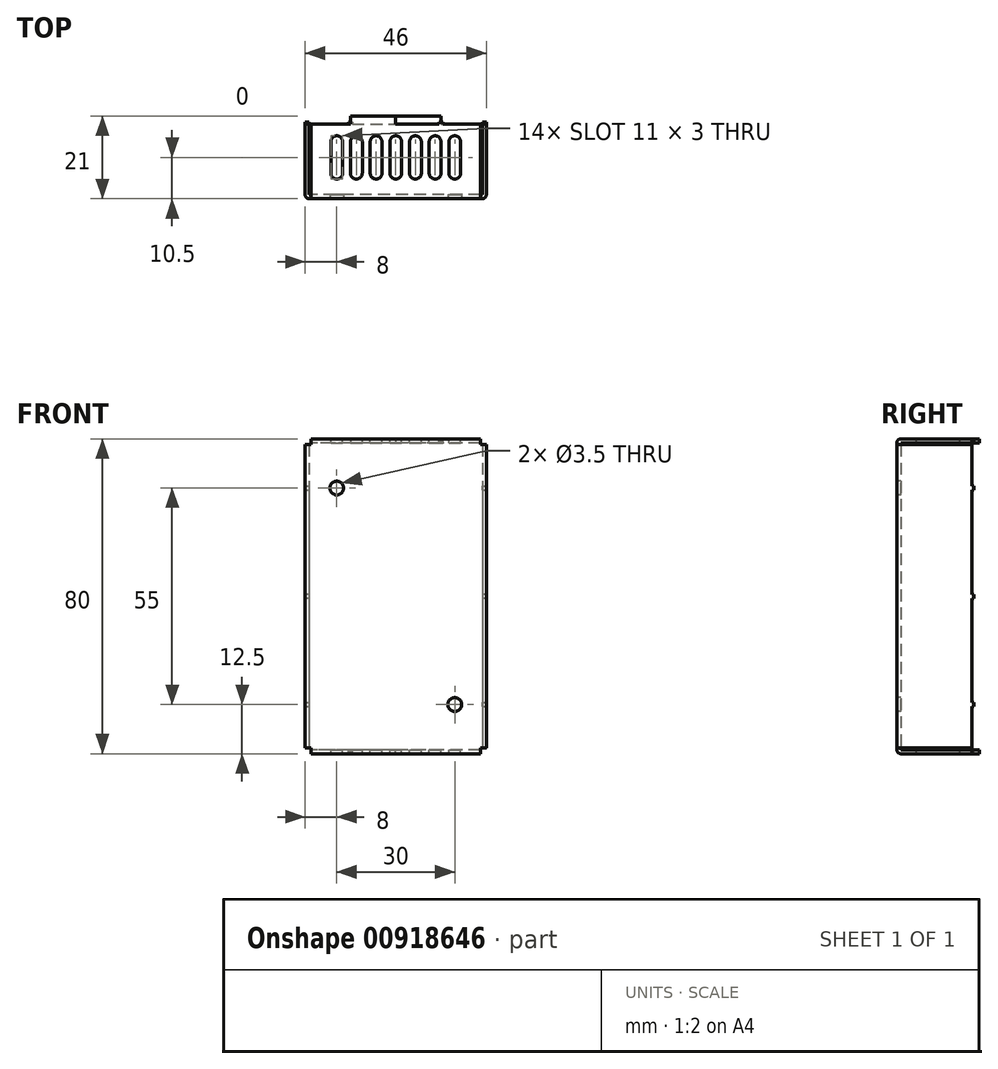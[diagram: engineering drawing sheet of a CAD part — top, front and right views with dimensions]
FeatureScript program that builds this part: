
annotation { "Feature Type Name" : "Feature", "Feature Type Description" : "" }
export const myFeature = defineFeature(function(context is Context, id is Id, definition is map)
    precondition{}
    {
        {
            var Q0;
            Q0=qCreatedBy(makeId("Front.planeOp"),FACE);
            var sketch = newSketch(context, id + "F0", { "sketchPlane" : qUnion([Q0])});
            skLineSegment(sketch, "E0.bottom", {"start": v(-23, 40) * mm, "end": v(23, 40) * mm});
            skLineSegment(sketch, "E0.top", {"start": v(-23, -40) * mm, "end": v(23, -40) * mm});
            skLineSegment(sketch, "E0.left", {"start": v(-23, 40) * mm, "end": v(-23, -40) * mm});
            skLineSegment(sketch, "E0.right", {"start": v(23, 40) * mm, "end": v(23, -40) * mm});
            skPoint(sketch, "E1", {"position": v(23, 0) * mm});
            skPoint(sketch, "E2", {"position": v(0, 40) * mm});
            skSolve(sketch);
        }
        {
            var Q0;
            Q0 = qSketchRegion(id + "F0", true);
            extrude(context, id + "F1", {"entities" : qUnion([Q0]), "oppositeDirection" : true, "depth" : 1 * mm, "offsetDistance" : 25 * mm});
        }
        {
            var Q0;
            Q0=makeQuery(id+"F1.opExtrude","CAP_FACE",FACE,{"disambiguationData":[OSD([sQuery(id+"F0.wireOp",EDGE,"E0.bottom"),sQuery(id+"F0.wireOp",EDGE,"E0.top"),sQuery(id+"F0.wireOp",EDGE,"E0.left"),sQuery(id+"F0.wireOp",EDGE,"E0.right")])],"isStart":false});
            var sketch = newSketch(context, id + "F2", { "sketchPlane" : qUnion([Q0])});
            skLineSegment(sketch, "E3.bottom", {"start": v(-21.5, 40) * mm, "end": v(21.5, 40) * mm});
            skLineSegment(sketch, "E3.top", {"start": v(-21.5, 39) * mm, "end": v(21.5, 39) * mm});
            skLineSegment(sketch, "E3.left", {"start": v(-21.5, 40) * mm, "end": v(-21.5, 39) * mm});
            skLineSegment(sketch, "E3.right", {"start": v(21.5, 40) * mm, "end": v(21.5, 39) * mm});
            skLineSegment(sketch, "E4.bottom", {"start": v(-23, 38.5) * mm, "end": v(-22, 38.5) * mm});
            skLineSegment(sketch, "E4.top", {"start": v(-23, -38.5) * mm, "end": v(-22, -38.5) * mm});
            skLineSegment(sketch, "E4.left", {"start": v(-23, 38.5) * mm, "end": v(-23, -38.5) * mm});
            skLineSegment(sketch, "E4.right", {"start": v(-22, 38.5) * mm, "end": v(-22, -38.5) * mm});
            skLineSegment(sketch, "E5.bottom", {"start": v(23, 38.5) * mm, "end": v(22, 38.5) * mm});
            skLineSegment(sketch, "E5.top", {"start": v(23, -38.5) * mm, "end": v(22, -38.5) * mm});
            skLineSegment(sketch, "E5.left", {"start": v(23, 38.5) * mm, "end": v(23, -38.5) * mm});
            skLineSegment(sketch, "E5.right", {"start": v(22, 38.5) * mm, "end": v(22, -38.5) * mm});
            skLineSegment(sketch, "E6.bottom", {"start": v(-21.5, -39) * mm, "end": v(21.5, -39) * mm});
            skLineSegment(sketch, "E6.top", {"start": v(-21.5, -40) * mm, "end": v(21.5, -40) * mm});
            skLineSegment(sketch, "E6.left", {"start": v(-21.5, -39) * mm, "end": v(-21.5, -40) * mm});
            skLineSegment(sketch, "E6.right", {"start": v(21.5, -39) * mm, "end": v(21.5, -40) * mm});
            skSolve(sketch);
        }
        {
            var Q0;
            Q0 = qSketchRegion(id + "F2", true);
            extrude(context, id + "F3", {"entities" : qUnion([Q0]), "operationType" : NewBodyOperationType.ADD, "depth" : 18 * mm, "offsetDistance" : 25 * mm});
        }
        {
            var Q0;
            Q0=makeQuery(id+"F1.opExtrude","CAP_FACE",FACE,{"disambiguationData":[OSD([sQuery(id+"F0.wireOp",EDGE,"E0.bottom"),sQuery(id+"F0.wireOp",EDGE,"E0.top"),sQuery(id+"F0.wireOp",EDGE,"E0.left"),sQuery(id+"F0.wireOp",EDGE,"E0.right")])],"isStart":false});
            var sketch = newSketch(context, id + "F4", { "sketchPlane" : qUnion([Q0])});
            skLineSegment(sketch, "E7.bottom", {"start": v(21.5, 40) * mm, "end": v(23, 40) * mm});
            skLineSegment(sketch, "E7.top", {"start": v(21.5, 38.5) * mm, "end": v(23, 38.5) * mm});
            skLineSegment(sketch, "E7.left", {"start": v(21.5, 40) * mm, "end": v(21.5, 38.5) * mm});
            skLineSegment(sketch, "E7.right", {"start": v(23, 40) * mm, "end": v(23, 38.5) * mm});
            skLineSegment(sketch, "E8.bottom", {"start": v(-23, 38.5) * mm, "end": v(-21.5, 38.5) * mm});
            skLineSegment(sketch, "E8.top", {"start": v(-23, 40) * mm, "end": v(-21.5, 40) * mm});
            skLineSegment(sketch, "E8.left", {"start": v(-23, 38.5) * mm, "end": v(-23, 40) * mm});
            skLineSegment(sketch, "E8.right", {"start": v(-21.5, 38.5) * mm, "end": v(-21.5, 40) * mm});
            skLineSegment(sketch, "E9.bottom", {"start": v(21.5, -40) * mm, "end": v(23, -40) * mm});
            skLineSegment(sketch, "E9.top", {"start": v(21.5, -38.5) * mm, "end": v(23, -38.5) * mm});
            skLineSegment(sketch, "E9.left", {"start": v(21.5, -40) * mm, "end": v(21.5, -38.5) * mm});
            skLineSegment(sketch, "E9.right", {"start": v(23, -40) * mm, "end": v(23, -38.5) * mm});
            skLineSegment(sketch, "E10.bottom", {"start": v(-23, -38.5) * mm, "end": v(-21.5, -38.5) * mm});
            skLineSegment(sketch, "E10.top", {"start": v(-23, -40) * mm, "end": v(-21.5, -40) * mm});
            skLineSegment(sketch, "E10.left", {"start": v(-23, -38.5) * mm, "end": v(-23, -40) * mm});
            skLineSegment(sketch, "E10.right", {"start": v(-21.5, -38.5) * mm, "end": v(-21.5, -40) * mm});
            skSolve(sketch);
        }
        {
            var Q0;
            Q0 = qSketchRegion(id + "F4", true);
            extrude(context, id + "F5", {"entities" : qUnion([Q0]), "operationType" : NewBodyOperationType.REMOVE, "endBound" : BoundingType.THROUGH_ALL, "oppositeDirection" : true, "depth" : 25 * mm, "offsetDistance" : 25 * mm});
        }
        {
            var Q0;
            Q0=makeQuery(id+"F1.opExtrude","CAP_FACE",FACE,{"disambiguationData":[OSD([sQuery(id+"F0.wireOp",EDGE,"E0.bottom"),sQuery(id+"F0.wireOp",EDGE,"E0.top"),sQuery(id+"F0.wireOp",EDGE,"E0.left"),sQuery(id+"F0.wireOp",EDGE,"E0.right")])],"isStart":true});
            var sketch = newSketch(context, id + "F6", { "sketchPlane" : qUnion([Q0])});
            skCircle(sketch, "E11", {"center": v(15, -27.5) * mm, "radius": 1.75 * mm});
            skCircle(sketch, "E12", {"center": v(-15, 27.5) * mm, "radius": 1.75 * mm});
            skSolve(sketch);
        }
        {
            var Q0;
            Q0 = qSketchRegion(id + "F6", true);
            extrude(context, id + "F7", {"entities" : qUnion([Q0]), "operationType" : NewBodyOperationType.REMOVE, "endBound" : BoundingType.THROUGH_ALL, "oppositeDirection" : true, "depth" : 25 * mm, "offsetDistance" : 25 * mm});
        }
        {
            var Q0;
            Q0=makeQuery(id+"F3.boolean.opBoolean","MERGE",FACE,{"derivedFrom":[makeQuery(id+"F1.opExtrude","SWEPT_FACE",FACE,{"disambiguationData":[OSD([sQuery(id+"F0.wireOp",EDGE,"E0.bottom")])]}),makeQuery(id+"F3.opExtrude","SWEPT_FACE",FACE,{"disambiguationData":[OSD([sQuery(id+"F2.wireOp",EDGE,"E3.bottom")])]})]});
            var sketch = newSketch(context, id + "F8", { "sketchPlane" : qUnion([Q0])});
            skLineSegment(sketch, "E13.left", {"start": v(1.5, 6.5) * mm, "end": v(1.5, 14.5) * mm});
            skLineSegment(sketch, "E13.right", {"start": v(-1.5, 6.5) * mm, "end": v(-1.5, 14.5) * mm});
            skArc(sketch, "E14", {"start": v(-1.5, 6.5) * mm, "mid": v(0, 5) * mm, "end": v(1.5, 6.5) * mm});
            skArc(sketch, "E15", {"start": v(1.5, 14.5) * mm, "mid": v(0, 16) * mm, "end": v(-1.5, 14.5) * mm});
            skPoint(sketch, "E16", {"position": v(0, 5) * mm});
            skPoint(sketch, "E17", {"position": v(0, 16) * mm});
            skLineSegment(sketch, "E18.left", {"start": v(-3.5, 6.5) * mm, "end": v(-3.5, 14.5) * mm});
            skLineSegment(sketch, "E18.right", {"start": v(-6.5, 6.5) * mm, "end": v(-6.5, 14.5) * mm});
            skArc(sketch, "E19", {"start": v(-6.5, 6.5) * mm, "mid": v(-5, 5) * mm, "end": v(-3.5, 6.5) * mm});
            skArc(sketch, "E20", {"start": v(-3.5, 14.5) * mm, "mid": v(-5, 16) * mm, "end": v(-6.5, 14.5) * mm});
            skPoint(sketch, "E21", {"position": v(-5, 5) * mm});
            skPoint(sketch, "E22", {"position": v(-5, 16) * mm});
            skLineSegment(sketch, "E23.left", {"start": v(-8.5, 6.5) * mm, "end": v(-8.5, 14.5) * mm});
            skLineSegment(sketch, "E23.right", {"start": v(-11.5, 6.5) * mm, "end": v(-11.5, 14.5) * mm});
            skArc(sketch, "E24", {"start": v(-11.5, 6.5) * mm, "mid": v(-10, 5) * mm, "end": v(-8.5, 6.5) * mm});
            skArc(sketch, "E25", {"start": v(-8.5, 14.5) * mm, "mid": v(-10, 16) * mm, "end": v(-11.5, 14.5) * mm});
            skPoint(sketch, "E26", {"position": v(-10, 5) * mm});
            skPoint(sketch, "E27", {"position": v(-10, 16) * mm});
            skLineSegment(sketch, "E28.left", {"start": v(-13.5, 6.5) * mm, "end": v(-13.5, 14.5) * mm});
            skLineSegment(sketch, "E28.right", {"start": v(-16.5, 6.5) * mm, "end": v(-16.5, 14.5) * mm});
            skArc(sketch, "E29", {"start": v(-16.5, 6.5) * mm, "mid": v(-15, 5) * mm, "end": v(-13.5, 6.5) * mm});
            skArc(sketch, "E30", {"start": v(-13.5, 14.5) * mm, "mid": v(-15, 16) * mm, "end": v(-16.5, 14.5) * mm});
            skPoint(sketch, "E31", {"position": v(-15, 5) * mm});
            skPoint(sketch, "E32", {"position": v(-15, 16) * mm});
            skLineSegment(sketch, "E33.left", {"start": v(11.5, 6.5) * mm, "end": v(11.5, 14.5) * mm});
            skLineSegment(sketch, "E33.right", {"start": v(8.5, 6.5) * mm, "end": v(8.5, 14.5) * mm});
            skArc(sketch, "E34", {"start": v(8.5, 6.5) * mm, "mid": v(10, 5) * mm, "end": v(11.5, 6.5) * mm});
            skArc(sketch, "E35", {"start": v(11.5, 14.5) * mm, "mid": v(10, 16) * mm, "end": v(8.5, 14.5) * mm});
            skPoint(sketch, "E36", {"position": v(10, 5) * mm});
            skPoint(sketch, "E37", {"position": v(10, 16) * mm});
            skLineSegment(sketch, "E38.left", {"start": v(6.5, 6.5) * mm, "end": v(6.5, 14.5) * mm});
            skLineSegment(sketch, "E38.right", {"start": v(3.5, 6.5) * mm, "end": v(3.5, 14.5) * mm});
            skArc(sketch, "E39", {"start": v(3.5, 6.5) * mm, "mid": v(5, 5) * mm, "end": v(6.5, 6.5) * mm});
            skArc(sketch, "E40", {"start": v(6.5, 14.5) * mm, "mid": v(5, 16) * mm, "end": v(3.5, 14.5) * mm});
            skPoint(sketch, "E41", {"position": v(5, 5) * mm});
            skPoint(sketch, "E42", {"position": v(5, 16) * mm});
            skLineSegment(sketch, "E43.left", {"start": v(16.5, 6.5) * mm, "end": v(16.5, 14.5) * mm});
            skLineSegment(sketch, "E43.right", {"start": v(13.5, 6.5) * mm, "end": v(13.5, 14.5) * mm});
            skArc(sketch, "E44", {"start": v(13.5, 6.5) * mm, "mid": v(15, 5) * mm, "end": v(16.5, 6.5) * mm});
            skArc(sketch, "E45", {"start": v(16.5, 14.5) * mm, "mid": v(15, 16) * mm, "end": v(13.5, 14.5) * mm});
            skPoint(sketch, "E46", {"position": v(15, 5) * mm});
            skPoint(sketch, "E47", {"position": v(15, 16) * mm});
            skSolve(sketch);
        }
        {
            var Q0;
            Q0 = qSketchRegion(id + "F8", true);
            extrude(context, id + "F9", {"entities" : qUnion([Q0]), "operationType" : NewBodyOperationType.REMOVE, "endBound" : BoundingType.THROUGH_ALL, "oppositeDirection" : true, "depth" : 25 * mm, "offsetDistance" : 25 * mm});
        }
        {
            var Q0;
            Q0=makeQuery(id+"F3.opExtrude","CAP_FACE",FACE,{"disambiguationData":[OSD([sQuery(id+"F2.wireOp",EDGE,"E6.bottom"),sQuery(id+"F2.wireOp",EDGE,"E6.top"),sQuery(id+"F2.wireOp",EDGE,"E6.left"),sQuery(id+"F2.wireOp",EDGE,"E6.right")])],"isStart":false});
            var sketch = newSketch(context, id + "F10", { "sketchPlane" : qUnion([Q0])});
            skLineSegment(sketch, "E48.bottom", {"start": v(0, -40) * mm, "end": v(-11.5, -40) * mm});
            skLineSegment(sketch, "E48.top", {"start": v(0, -39) * mm, "end": v(-11.5, -39) * mm});
            skLineSegment(sketch, "E48.left", {"start": v(0, -40) * mm, "end": v(0, -39) * mm});
            skLineSegment(sketch, "E48.right", {"start": v(-11.5, -40) * mm, "end": v(-11.5, -39) * mm});
            skLineSegment(sketch, "E49.bottom", {"start": v(0, 40) * mm, "end": v(11.5, 40) * mm});
            skLineSegment(sketch, "E49.top", {"start": v(0, 39) * mm, "end": v(11.5, 39) * mm});
            skLineSegment(sketch, "E49.left", {"start": v(0, 40) * mm, "end": v(0, 39) * mm});
            skLineSegment(sketch, "E49.right", {"start": v(11.5, 40) * mm, "end": v(11.5, 39) * mm});
            skSolve(sketch);
        }
        {
            var Q0;
            Q0 = qSketchRegion(id + "F10", true);
            extrude(context, id + "F11", {"entities" : qUnion([Q0]), "operationType" : NewBodyOperationType.ADD, "depth" : 2 * mm, "offsetDistance" : 25 * mm});
        }
        {
            var Q0;
            Q0=makeQuery(id+"F3.opExtrude","CAP_FACE",FACE,{"disambiguationData":[OSD([sQuery(id+"F2.wireOp",EDGE,"E5.bottom"),sQuery(id+"F2.wireOp",EDGE,"E5.top"),sQuery(id+"F2.wireOp",EDGE,"E5.left"),sQuery(id+"F2.wireOp",EDGE,"E5.right")])],"isStart":false});
            var sketch = newSketch(context, id + "F12", { "sketchPlane" : qUnion([Q0])});
            skLineSegment(sketch, "E50.bottom", {"start": v(12, -40) * mm, "end": v(11, -40) * mm});
            skLineSegment(sketch, "E50.top", {"start": v(12, -39) * mm, "end": v(11, -39) * mm});
            skLineSegment(sketch, "E50.left", {"start": v(12, -40) * mm, "end": v(12, -39) * mm});
            skLineSegment(sketch, "E50.right", {"start": v(11, -40) * mm, "end": v(11, -39) * mm});
            skLineSegment(sketch, "E51.bottom", {"start": v(-11, 39) * mm, "end": v(-12, 39) * mm});
            skLineSegment(sketch, "E51.top", {"start": v(-11, 40) * mm, "end": v(-12, 40) * mm});
            skLineSegment(sketch, "E51.left", {"start": v(-11, 39) * mm, "end": v(-11, 40) * mm});
            skLineSegment(sketch, "E51.right", {"start": v(-12, 39) * mm, "end": v(-12, 40) * mm});
            skLineSegment(sketch, "E52.bottom", {"start": v(23, 27) * mm, "end": v(22, 27) * mm});
            skLineSegment(sketch, "E52.top", {"start": v(23, 28) * mm, "end": v(22, 28) * mm});
            skLineSegment(sketch, "E52.left", {"start": v(23, 27) * mm, "end": v(23, 28) * mm});
            skLineSegment(sketch, "E52.right", {"start": v(22, 27) * mm, "end": v(22, 28) * mm});
            skLineSegment(sketch, "E53.bottom", {"start": v(-22, 27) * mm, "end": v(-23, 27) * mm});
            skLineSegment(sketch, "E53.top", {"start": v(-22, 28) * mm, "end": v(-23, 28) * mm});
            skLineSegment(sketch, "E53.left", {"start": v(-22, 27) * mm, "end": v(-22, 28) * mm});
            skLineSegment(sketch, "E53.right", {"start": v(-23, 27) * mm, "end": v(-23, 28) * mm});
            skLineSegment(sketch, "E54.bottom", {"start": v(23, -28) * mm, "end": v(22, -28) * mm});
            skLineSegment(sketch, "E54.top", {"start": v(23, -27) * mm, "end": v(22, -27) * mm});
            skLineSegment(sketch, "E54.left", {"start": v(23, -28) * mm, "end": v(23, -27) * mm});
            skLineSegment(sketch, "E54.right", {"start": v(22, -28) * mm, "end": v(22, -27) * mm});
            skLineSegment(sketch, "E55.bottom", {"start": v(-22, -28) * mm, "end": v(-23, -28) * mm});
            skLineSegment(sketch, "E55.top", {"start": v(-22, -27) * mm, "end": v(-23, -27) * mm});
            skLineSegment(sketch, "E55.left", {"start": v(-22, -28) * mm, "end": v(-22, -27) * mm});
            skLineSegment(sketch, "E55.right", {"start": v(-23, -28) * mm, "end": v(-23, -27) * mm});
            skPoint(sketch, "E56", {"position": v(11.5, -39) * mm});
            skPoint(sketch, "E57", {"position": v(-11.5, 39) * mm});
            skPoint(sketch, "E58", {"position": v(22, 27.5) * mm});
            skPoint(sketch, "E59.positionSnap0", {"position": v(-22, 27.5) * mm});
            skPoint(sketch, "E60", {"position": v(-22, -27.5) * mm});
            skPoint(sketch, "E61", {"position": v(22, -27.5) * mm});
            skPoint(sketch, "E62", {"position": v(15, 27.5) * mm});
            skLineSegment(sketch, "E63.bottom", {"start": v(22, 0.5) * mm, "end": v(23, 0.5) * mm});
            skLineSegment(sketch, "E63.top", {"start": v(22, -0.5) * mm, "end": v(23, -0.5) * mm});
            skLineSegment(sketch, "E63.left", {"start": v(22, 0.5) * mm, "end": v(22, -0.5) * mm});
            skLineSegment(sketch, "E63.right", {"start": v(23, 0.5) * mm, "end": v(23, -0.5) * mm});
            skLineSegment(sketch, "E64.bottom", {"start": v(-23, 0.5) * mm, "end": v(-22, 0.5) * mm});
            skLineSegment(sketch, "E64.top", {"start": v(-23, -0.5) * mm, "end": v(-22, -0.5) * mm});
            skLineSegment(sketch, "E64.left", {"start": v(-23, 0.5) * mm, "end": v(-23, -0.5) * mm});
            skLineSegment(sketch, "E64.right", {"start": v(-22, 0.5) * mm, "end": v(-22, -0.5) * mm});
            skPoint(sketch, "E65", {"position": v(-22, 0) * mm});
            skPoint(sketch, "E66", {"position": v(22, 0) * mm});
            skPoint(sketch, "E67", {"position": v(-15, -27.5) * mm});
            skSolve(sketch);
        }
        {
            var Q0;
            Q0 = qSketchRegion(id + "F12", true);
            extrude(context, id + "F13", {"entities" : qUnion([Q0]), "operationType" : NewBodyOperationType.ADD, "depth" : 0.5 * mm, "offsetDistance" : 25 * mm});
        }
        {
            var Q0;
            Q0=makeQuery(id+"F1.opExtrude","CAP_EDGE",EDGE,{"disambiguationData":[OSD([sQuery(id+"F0.wireOp",EDGE,"E0.left")])],"isStart":true});
            var Q1;
            Q1=makeQuery(id+"F1.opExtrude","CAP_EDGE",EDGE,{"disambiguationData":[OSD([sQuery(id+"F0.wireOp",EDGE,"E0.bottom")])],"isStart":true});
            var Q2;
            Q2=makeQuery(id+"F1.opExtrude","CAP_EDGE",EDGE,{"disambiguationData":[OSD([sQuery(id+"F0.wireOp",EDGE,"E0.right")])],"isStart":true});
            var Q3;
            Q3=makeQuery(id+"F1.opExtrude","CAP_EDGE",EDGE,{"disambiguationData":[OSD([sQuery(id+"F0.wireOp",EDGE,"E0.top")])],"isStart":true});
            fillet(context, id + "F14", {"entities" : qUnion([Q0, Q1, Q2, Q3]), "radius" : 1 * mm, "tangentPropagation" : true, "allowEdgeOverflow" : false});
        }
    });
